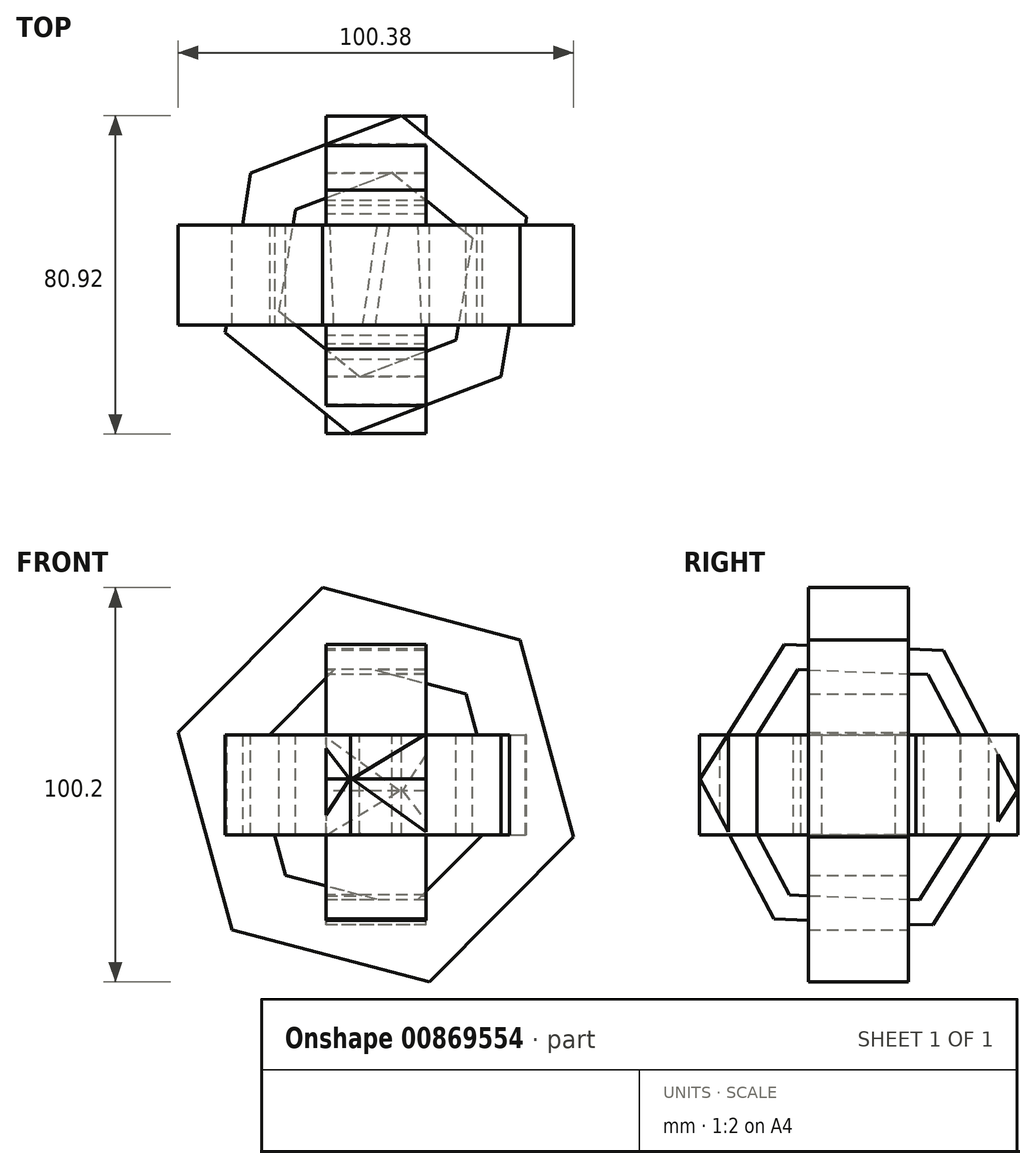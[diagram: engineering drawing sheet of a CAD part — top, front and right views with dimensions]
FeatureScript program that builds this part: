
annotation { "Feature Type Name" : "Feature", "Feature Type Description" : "" }
export const myFeature = defineFeature(function(context is Context, id is Id, definition is map)
    precondition{}
    {
        {
            var Q0;
            Q0=qCreatedBy(makeId("Top.planeOp"),FACE);
            var sketch = newSketch(context, id + "F0", { "sketchPlane" : qUnion([Q0])});
            skCircle(sketch, "E0.cCircle", {"center": v(0, 0) * mm, "radius": 22.75 * mm, "construction": true});
            skLineSegment(sketch, "E0.0", {"start": v(-4.16, -25.94) * mm, "end": v(-24.54, -9.36) * mm});
            skLineSegment(sketch, "E0.1", {"start": v(-24.54, -9.36) * mm, "end": v(-20.38, 16.57) * mm});
            skLineSegment(sketch, "E0.2", {"start": v(-20.38, 16.57) * mm, "end": v(4.16, 25.94) * mm});
            skLineSegment(sketch, "E0.3", {"start": v(4.16, 25.94) * mm, "end": v(24.54, 9.36) * mm});
            skLineSegment(sketch, "E0.4", {"start": v(24.54, 9.36) * mm, "end": v(20.38, -16.57) * mm});
            skLineSegment(sketch, "E0.5", {"start": v(20.38, -16.57) * mm, "end": v(-4.16, -25.94) * mm});
            skPoint(sketch, "E0.0.midPoint", {"position": v(-14.35, -17.65) * mm});
            skCircle(sketch, "E1.cCircle", {"center": v(0, 0) * mm, "radius": 35.49 * mm, "construction": true});
            skLineSegment(sketch, "E1.0", {"start": v(-6.5, -40.46) * mm, "end": v(-38.29, -14.6) * mm});
            skLineSegment(sketch, "E1.1", {"start": v(-38.29, -14.6) * mm, "end": v(-31.8, 25.85) * mm});
            skLineSegment(sketch, "E1.2", {"start": v(-31.8, 25.85) * mm, "end": v(6.5, 40.46) * mm});
            skLineSegment(sketch, "E1.3", {"start": v(6.5, 40.46) * mm, "end": v(38.29, 14.6) * mm});
            skLineSegment(sketch, "E1.4", {"start": v(38.29, 14.6) * mm, "end": v(31.8, -25.85) * mm});
            skLineSegment(sketch, "E1.5", {"start": v(31.8, -25.85) * mm, "end": v(-6.5, -40.46) * mm});
            skPoint(sketch, "E1.0.midPoint", {"position": v(-22.39, -27.54) * mm});
            skSolve(sketch);
        }
        {
            var Q0;
            Q0 = qSketchRegion(id + "F0", true);
            extrude(context, id + "F1", {"entities" : qUnion([Q0]), "endBound" : BoundingType.SYMMETRIC, "oppositeDirection" : true, "depth" : 25.4 * mm, "offsetDistance" : 25.4 * mm});
        }
        {
            var Q0;
            Q0=qCreatedBy(makeId("Front.planeOp"),FACE);
            var sketch = newSketch(context, id + "F2", { "sketchPlane" : qUnion([Q0])});
            skCircle(sketch, "E2.cCircle", {"center": v(0, 0) * mm, "radius": 28.13 * mm, "construction": true});
            skLineSegment(sketch, "E2.0", {"start": v(8.51, -31.35) * mm, "end": v(-22.9, -23.05) * mm});
            skLineSegment(sketch, "E2.1", {"start": v(-22.9, -23.05) * mm, "end": v(-31.4, 8.3) * mm});
            skLineSegment(sketch, "E2.2", {"start": v(-31.4, 8.3) * mm, "end": v(-8.51, 31.35) * mm});
            skLineSegment(sketch, "E2.3", {"start": v(-8.51, 31.35) * mm, "end": v(22.9, 23.05) * mm});
            skLineSegment(sketch, "E2.4", {"start": v(22.9, 23.05) * mm, "end": v(31.4, -8.3) * mm});
            skLineSegment(sketch, "E2.5", {"start": v(31.4, -8.3) * mm, "end": v(8.51, -31.35) * mm});
            skPoint(sketch, "E2.0.midPoint", {"position": v(-7.2, -27.2) * mm});
            skCircle(sketch, "E3.cCircle", {"center": v(0, 0) * mm, "radius": 44.96 * mm, "construction": true});
            skLineSegment(sketch, "E3.0", {"start": v(13.6, -50.1) * mm, "end": v(-36.59, -36.83) * mm});
            skLineSegment(sketch, "E3.1", {"start": v(-36.59, -36.83) * mm, "end": v(-50.2, 13.27) * mm});
            skLineSegment(sketch, "E3.2", {"start": v(-50.2, 13.27) * mm, "end": v(-13.6, 50.1) * mm});
            skLineSegment(sketch, "E3.3", {"start": v(-13.6, 50.1) * mm, "end": v(36.59, 36.83) * mm});
            skLineSegment(sketch, "E3.4", {"start": v(36.59, 36.83) * mm, "end": v(50.2, -13.27) * mm});
            skLineSegment(sketch, "E3.5", {"start": v(50.2, -13.27) * mm, "end": v(13.6, -50.1) * mm});
            skPoint(sketch, "E3.0.midPoint", {"position": v(-11.5, -43.47) * mm});
            skSolve(sketch);
        }
        {
            var Q0;
            Q0=makeQuery(id+"F2.imprint","IMPRINT",FACE,{"disambiguationData":[TD([[makeQuery(id+"F2.imprint","IMPRINT",EDGE,{"derivedFrom":sQuery(id+"F2.wireOp",EDGE,"E2.0")}),1.0]])]});
            extrude(context, id + "F3", {"entities" : qUnion([Q0]), "operationType" : NewBodyOperationType.ADD, "endBound" : BoundingType.SYMMETRIC, "depth" : 25.4 * mm, "offsetDistance" : 25.4 * mm});
        }
        {
            var Q0;
            Q0=qCreatedBy(makeId("Right.planeOp"),FACE);
            var sketch = newSketch(context, id + "F4", { "sketchPlane" : qUnion([Q0])});
            skCircle(sketch, "E4.cCircle", {"center": v(0, 0) * mm, "radius": 28.65 * mm, "construction": true});
            skLineSegment(sketch, "E4.0", {"start": v(-33.06, 1.27) * mm, "end": v(-15.43, 29.26) * mm});
            skLineSegment(sketch, "E4.1", {"start": v(-15.43, 29.26) * mm, "end": v(17.63, 28) * mm});
            skLineSegment(sketch, "E4.2", {"start": v(17.63, 28) * mm, "end": v(33.06, -1.27) * mm});
            skLineSegment(sketch, "E4.3", {"start": v(33.06, -1.27) * mm, "end": v(15.43, -29.26) * mm});
            skLineSegment(sketch, "E4.4", {"start": v(15.43, -29.26) * mm, "end": v(-17.63, -28) * mm});
            skLineSegment(sketch, "E4.5", {"start": v(-17.63, -28) * mm, "end": v(-33.06, 1.27) * mm});
            skPoint(sketch, "E4.0.midPoint", {"position": v(-24.25, 15.27) * mm});
            skCircle(sketch, "E5.cCircle", {"center": v(0, 0) * mm, "radius": 34.91 * mm, "construction": true});
            skLineSegment(sketch, "E5.0", {"start": v(-40.28, 1.54) * mm, "end": v(-18.8, 35.66) * mm});
            skLineSegment(sketch, "E5.1", {"start": v(-18.8, 35.66) * mm, "end": v(21.48, 34.11) * mm});
            skLineSegment(sketch, "E5.2", {"start": v(21.48, 34.11) * mm, "end": v(40.28, -1.54) * mm});
            skLineSegment(sketch, "E5.3", {"start": v(40.28, -1.54) * mm, "end": v(18.8, -35.66) * mm});
            skLineSegment(sketch, "E5.4", {"start": v(18.8, -35.66) * mm, "end": v(-21.48, -34.11) * mm});
            skLineSegment(sketch, "E5.5", {"start": v(-21.48, -34.11) * mm, "end": v(-40.28, 1.54) * mm});
            skPoint(sketch, "E5.0.midPoint", {"position": v(-29.54, 18.6) * mm});
            skSolve(sketch);
        }
        {
            var Q0;
            Q0 = qSketchRegion(id + "F4", true);
            extrude(context, id + "F5", {"entities" : qUnion([Q0]), "operationType" : NewBodyOperationType.ADD, "endBound" : BoundingType.SYMMETRIC, "depth" : 25.4 * mm, "offsetDistance" : 25.4 * mm});
        }
    });
